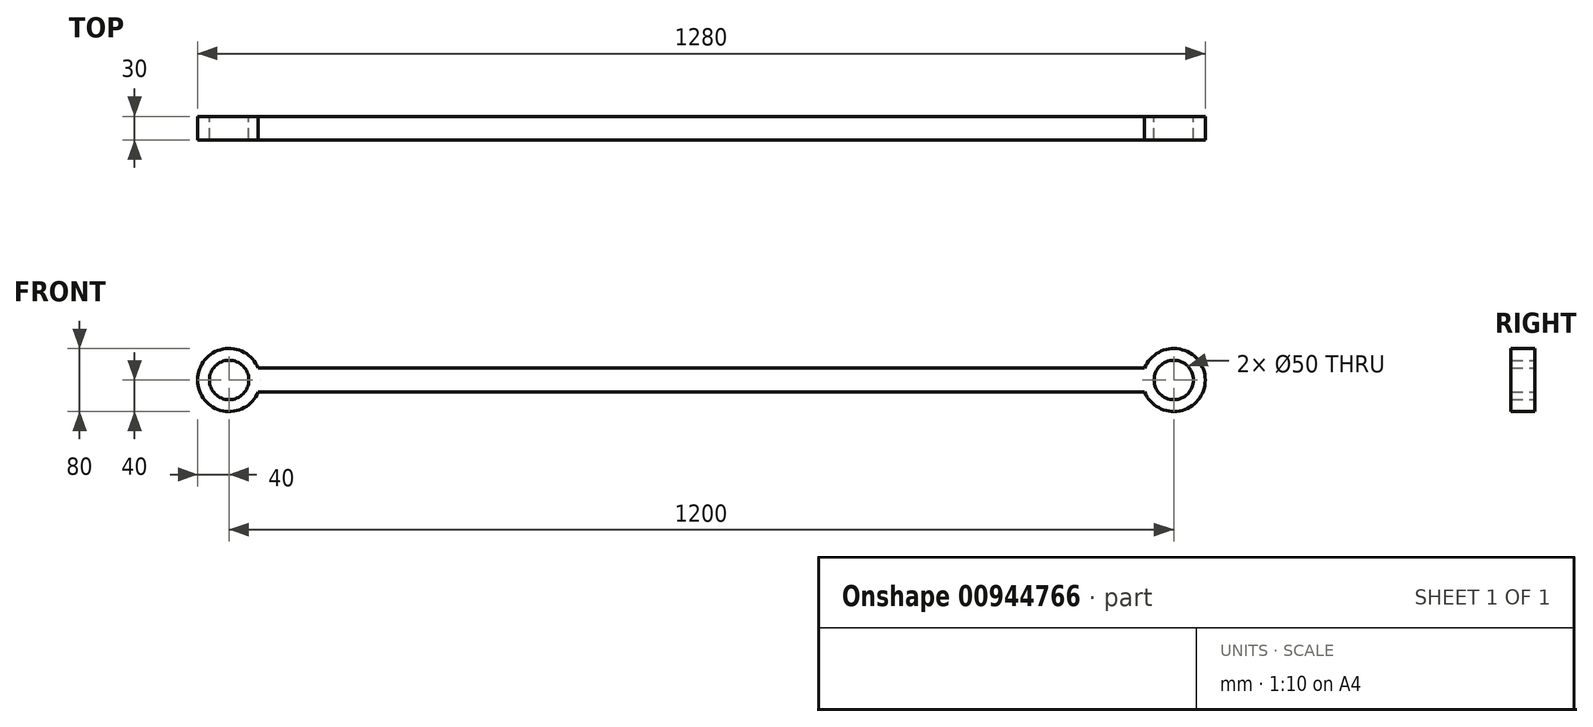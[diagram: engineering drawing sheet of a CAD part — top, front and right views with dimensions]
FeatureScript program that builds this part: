
annotation { "Feature Type Name" : "Feature", "Feature Type Description" : "" }
export const myFeature = defineFeature(function(context is Context, id is Id, definition is map)
    precondition{}
    {
        {
            var Q0;
            Q0=qCreatedBy(makeId("Front.planeOp"),FACE);
            var sketch = newSketch(context, id + "F0", { "sketchPlane" : qUnion([Q0])});
            skCircle(sketch, "E0", {"center": v(-600, 0) * mm, "radius": 25 * mm});
            skCircle(sketch, "E1", {"center": v(600, 0) * mm, "radius": 25 * mm});
            skArc(sketch, "E2", {"start": v(-562.92, 15) * mm, "mid": v(-640, 0) * mm, "end": v(-562.92, -15) * mm});
            skArc(sketch, "E3", {"start": v(562.92, -15) * mm, "mid": v(640, 0) * mm, "end": v(562.92, 15) * mm});
            skLineSegment(sketch, "E4.bottom", {"start": v(562.92, -15) * mm, "end": v(-562.92, -15) * mm});
            skLineSegment(sketch, "E4.top", {"start": v(562.92, 15) * mm, "end": v(-562.92, 15) * mm});
            skLineSegment(sketch, "E4.left", {"start": v(562.92, -15) * mm, "end": v(562.92, 15) * mm, "construction": true});
            skLineSegment(sketch, "E4.right", {"start": v(-562.92, -15) * mm, "end": v(-562.92, 15) * mm, "construction": true});
            skPoint(sketch, "E4.middle", {"position": v(0, 0) * mm});
            skLineSegment(sketch, "E5", {"start": v(-250.43, 0) * mm, "end": v(205.1, 0) * mm, "construction": true});
            skSolve(sketch);
        }
        {
            var Q0;
            Q0=qSketchRegion(id+"F0",true);
            extrude(context, id + "F1", {"entities" : qUnion([Q0]), "endBound" : BoundingType.SYMMETRIC, "depth" : 30 * mm, "offsetDistance" : 25 * mm});
        }
    });
